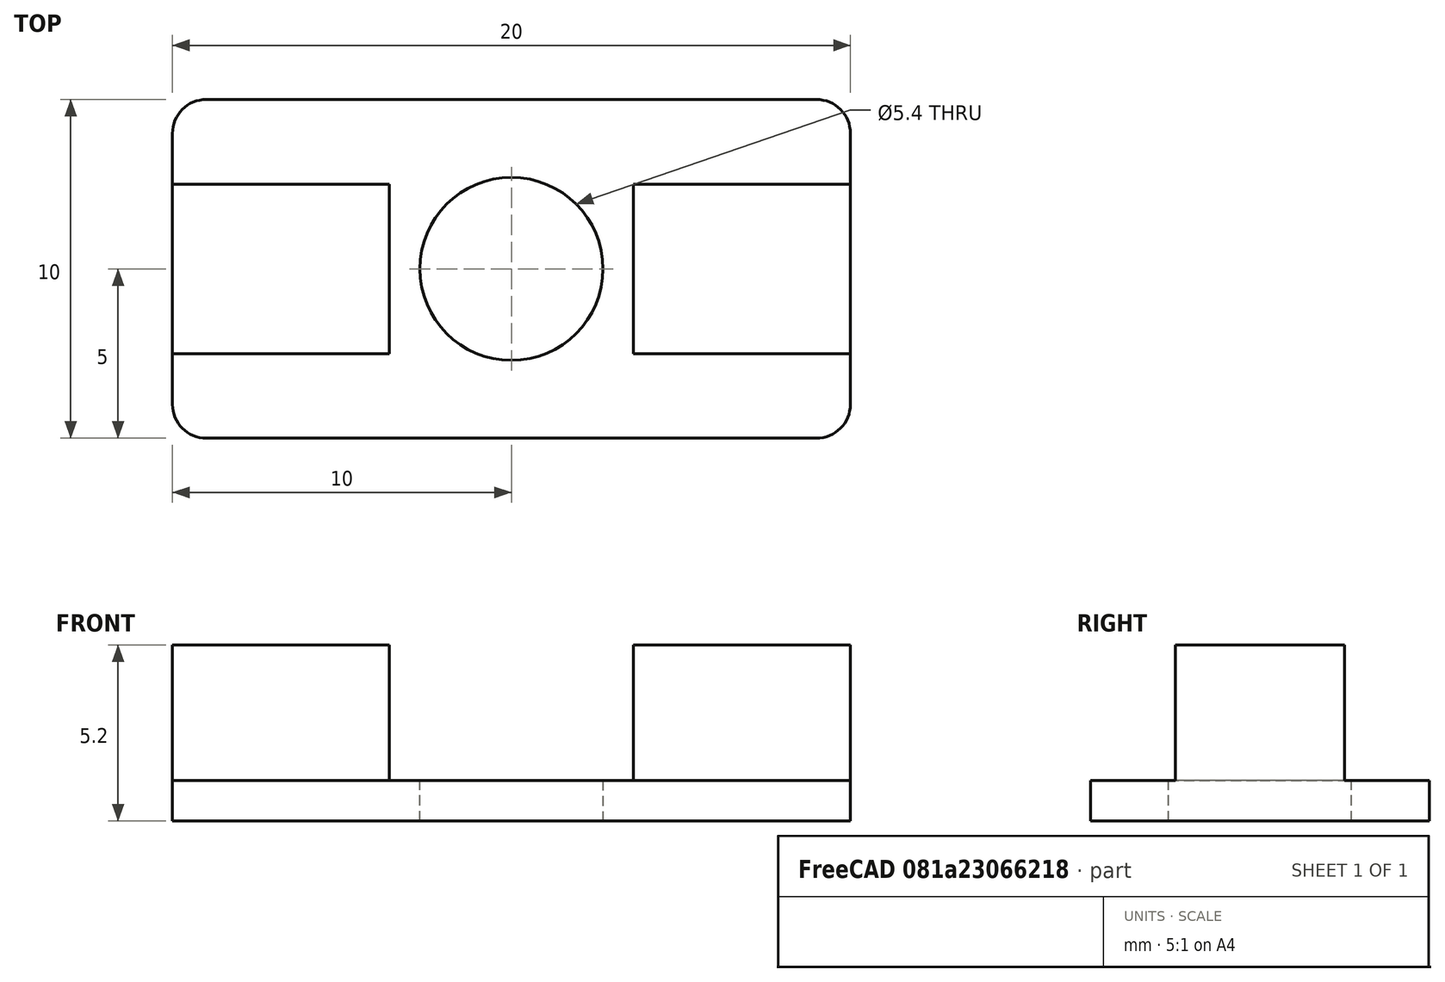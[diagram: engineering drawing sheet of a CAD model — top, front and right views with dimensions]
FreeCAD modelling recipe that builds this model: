
FCSTD DOCUMENT  (FreeCAD 0.18R)
Label: Centerplate2020I
License: CreativeCommons Attribution
LicenseURL: http://creativecommons.org/licenses/by/4.0/
objects: Sketcher::SketchObject×3, PartDesign::Pad×2, PartDesign::Pocket×1, PartDesign::Mirrored×1, PartDesign::Fillet×1, PartDesign::Body×1, App::Part×1, Mesh::Feature×1
note: 12 computed .brp shape members not serialized (recipe doc carries the construction recipe); baked Part::Feature solids carry a one-line shape summary decoded from their .brp

FEATURE [Sketcher::SketchObject] Sketch
  MapMode = 5
  Support = -> [XY_Plane]
  sketch-geometry (4):
    g0: LineSegment StartX=-10 StartY=5 StartZ=0 EndX=10 EndY=5 EndZ=0
    g1: LineSegment StartX=10 StartY=5 StartZ=0 EndX=10 EndY=-5 EndZ=0
    g2: LineSegment StartX=10 StartY=-5 StartZ=0 EndX=-10 EndY=-5 EndZ=0
    g3: LineSegment StartX=-10 StartY=-5 StartZ=0 EndX=-10 EndY=5 EndZ=0
  constraints (10):
    c: Coincident(g0,g1)
    c: Coincident(g1,g2)
    c: Coincident(g2,g3)
    c: Coincident(g3,g0)
    c: Horizontal(g2)
    c: Vertical(g1)
    c: Symmetric(g0,g0,g-2)
    c: Symmetric(g0,g2,g-1)
    c: DistanceY(g3,g3) = 10
    c: DistanceX(g0,g0) = 20
FEATURE [PartDesign::Pad] Pad
  Length = 1.2
  Length2 = 100
  Profile = -> Sketch
  Type = 0
FEATURE [Sketcher::SketchObject] Sketch001
  MapMode = 5
  Placement = pos=(0,0,1.2) rot=(0,0,1;0rad)
  Support = -> [Pad]
  sketch-geometry (4):
    g0: LineSegment StartX=-10 StartY=2.5 StartZ=0 EndX=-3.6 EndY=2.5 EndZ=0
    g1: LineSegment StartX=-3.6 StartY=2.5 StartZ=0 EndX=-3.6 EndY=-2.5 EndZ=0
    g2: LineSegment StartX=-3.6 StartY=-2.5 StartZ=0 EndX=-10 EndY=-2.5 EndZ=0
    g3: LineSegment StartX=-10 StartY=-2.5 StartZ=0 EndX=-10 EndY=2.5 EndZ=0
  constraints (11):
    c: Coincident(g0,g1)
    c: Coincident(g1,g2)
    c: Coincident(g2,g3)
    c: Coincident(g3,g0)
    c: Horizontal(g2)
    c: Vertical(g1)
    c: Symmetric(g2,g0,g-1)
    c: DistanceX(g0,g0) = 6.4
    c: DistanceY(g3,g3) = 5
    c: Horizontal(g0)
    c: DistanceX(g0,g-1) = 3.6
FEATURE [PartDesign::Pad] Pad001
  BaseFeature = -> Pad
  Length = 4
  Length2 = 100
  Profile = -> Sketch001
  Type = 0
FEATURE [Sketcher::SketchObject] Sketch002
  MapMode = 5
  Placement = pos=(0,0,1.2) rot=(0,0,1;0rad)
  Support = -> [Pad001]
  sketch-geometry (1):
    g0: Circle CenterX=0 CenterY=0 CenterZ=0 NormalX=0 NormalY=0 NormalZ=1 AngleXU=0 Radius=2.7
  constraints (2):
    c: Coincident(g0,g-1)
    c: Radius(g0) = 2.7
FEATURE [PartDesign::Pocket] Pocket
  BaseFeature = -> Pad001
  Length = 10
  Length2 = 100
  Midplane = true
  Profile = -> Sketch002
  Type = 0
FEATURE [PartDesign::Mirrored] Mirrored
  BaseFeature = -> Pocket
  MirrorPlane = -> Sketch001 [V_Axis]
  Originals = -> [Pad001]
FEATURE [PartDesign::Fillet] Fillet
  Base = -> Mirrored [Edge2,Edge1,Edge5,Edge10]
  BaseFeature = -> Mirrored
  Radius = 1
FEATURE [PartDesign::Body] Body  label="Centerplate 20x20 Slot5 Extrusion (Type I)"
  Group = -> [Sketch,Pad,Sketch001,Pad001,Sketch002,Pocket,Mirrored,Fillet]
  Origin = -> Origin
  Tip = -> Fillet
FEATURE [App::Part] Part  label="Centerplate"
  Group = -> [Body]
  Origin = -> Origin001
FEATURE [Mesh::Feature] Mesh  label="Centerplate 20x20 Slot5 Extrusion (Type I) (Meshed)"
